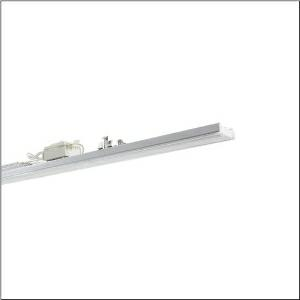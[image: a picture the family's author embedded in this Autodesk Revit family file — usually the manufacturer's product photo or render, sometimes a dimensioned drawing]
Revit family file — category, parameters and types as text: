
# Revit family: licross_r__21_recessed_ho_52te12dn4fxm_2e24
name_source: partatom
category: Lighting Fixtures
units: mm (PartAtom-declared; Revit-internal decimal feet)

## family parameters
Cut with Voids When Loaded = No
Host = Face
Light Source = No
Part Type = Normal
Room Calculation Point = No
Round Connector Dimension = Use Diameter
Shared = No

## types (1)
- --- (1 x LED, 15000 lm, 84.6 W, 4000K)
    Apparent Load = 85 VA
    CIE Flux Codes = 69 91 98 100 100
    Color Rendering = 80
    Color Temperature = 4000K
    Default Elevation = 1800 mm
    Description = Licross® 21 Recessed HO, luminaire insert, of sheet steel, galvanised, coil coated, white, length: 1.500mm, width: 66mm, height: 67mm, LED rated luminous flux: 15.000lm, light colour: 840, control gear: DALI 2, with plug, 5-pole, with phase selection, mains connection: 220..240V, AC, 50/60Hz, rated input power: 85W, internal wiring halogen-free, primary optical cover: cover, of PMMA, light emission: direct distribution, primary light characteristic: symmetric, protection rating (complete): IP54, insulation class (complete): insulation class I (protective earthing), certification: CE, ENEC, VDE, UKCA, protection symbol: D if used in an environment with non-conductive dust loads with corresponding accessories, impact resistance: IK06, permissible ambient temperature for indoor applications: -25..+30°C, corresponds to IFS (International Featured Standards) requirements for safety and quality in the food industry, reducing of maximum allowable ambient temperature of 5°C with ceiling mounting, LABS conformity tested according to VDMA 24364:2018-05, packaging unit: 1 piece
    Height = 58 mm
    Lamp = 1 x LED
    Lamp Light Flux = 15000 lm
    Lamp Power = 84.6 W
    Lamp count = 1
    Length = 1500 mm
    Luminous efficacy = 177 lm/W
    Manufacturer = Siteco
    ModVariant = No
    Model = 52TE12DN4FXM
    Mounting Place = Ceiling
    Mounting Type = Pendant
    Number of Poles = 1
    OnlyDefault = Yes
    Power Factor = 1
    Product Name = Licross® 21 Recessed HO
    Product group = luminaire insert | ceiling pendant
    ProductGroupID = 902
    Protection Class = Protection class I
    Protection Degree = IP 54
    RLX_Detail_Level = 1
    RLX_Emergency_Light_Flux = 0 lm
    RLX_Emergency_Type = 0
    RLX_Emergency_Type_DB = No
    RlxData = <blob elided: 24753 chars, md5=a2732833>
    Socket = socket
    Standby Power = 0 W
    System Light Flux = 15000 lm
    System Power = 85 W
    Type Comments = factory setting: luminous flux: 100 % | dim-lin: 254 | 484 mA
    Type Image = l_1296930.jpg
    URL = http://relux.com
    VarID = @adj_137955
    Voltage = 0 V
    Weight = 0.00 kg
    Width = 66 mm

## geometry (parser evidence)
native form markers: Blend x4, Sweep x11
no freeform markers — native parametric forms only
